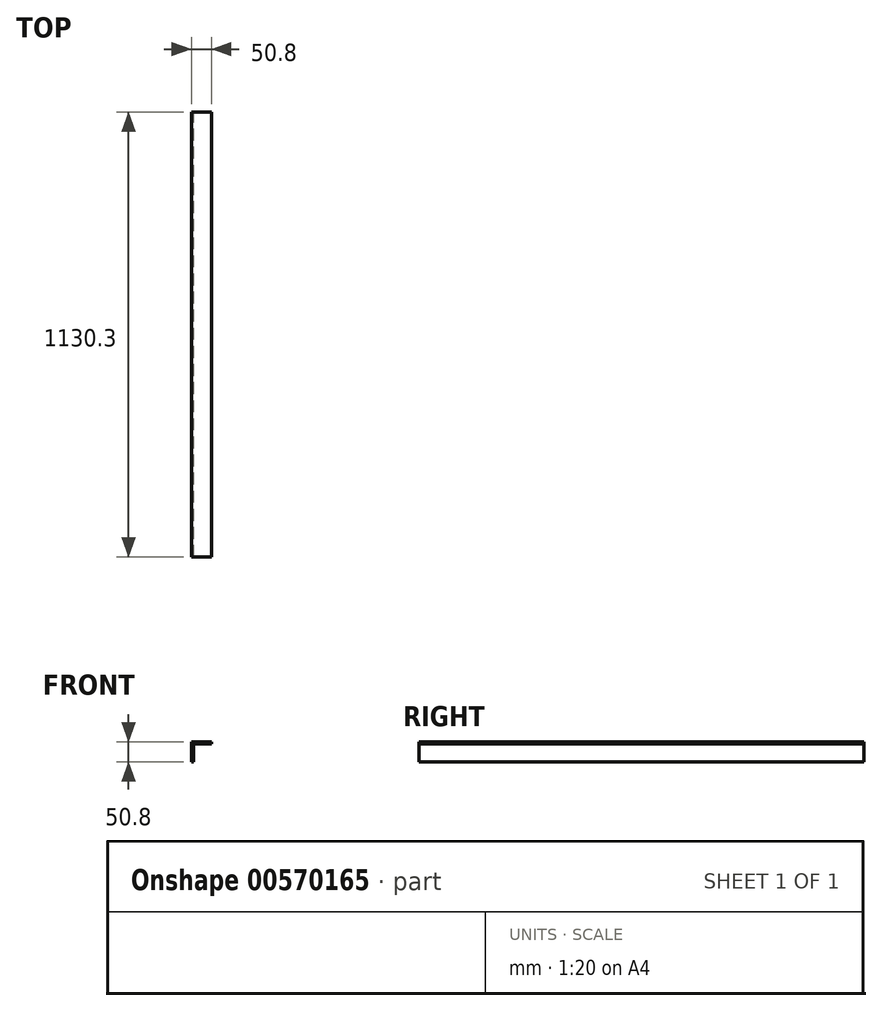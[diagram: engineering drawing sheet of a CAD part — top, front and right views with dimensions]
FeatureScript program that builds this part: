
annotation { "Feature Type Name" : "Feature", "Feature Type Description" : "" }
export const myFeature = defineFeature(function(context is Context, id is Id, definition is map)
    precondition{}
    {
        {
            var Q0;
            Q0=qCreatedBy(makeId("Front.planeOp"),FACE);
            var sketch = newSketch(context, id + "F0", { "sketchPlane" : qUnion([Q0])});
            skLineSegment(sketch, "E0", {"start": v(0, 0) * mm, "end": v(0, 50.8) * mm});
            skLineSegment(sketch, "E1", {"start": v(0, 50.8) * mm, "end": v(50.8, 50.8) * mm});
            skLineSegment(sketch, "E2", {"start": v(50.8, 50.8) * mm, "end": v(50.8, 46.04) * mm});
            skLineSegment(sketch, "E3", {"start": v(50.8, 46.04) * mm, "end": v(4.76, 46.04) * mm});
            skLineSegment(sketch, "E4", {"start": v(4.76, 46.04) * mm, "end": v(4.76, 0) * mm});
            skLineSegment(sketch, "E5", {"start": v(4.76, 0) * mm, "end": v(0, 0) * mm});
            skSolve(sketch);
        }
        {
            var Q0;
            Q0=makeQuery(id+"F0.imprint","IMPRINT",FACE,{"disambiguationData":[TD([[makeQuery(id+"F0.imprint","IMPRINT",EDGE,{"derivedFrom":sQuery(id+"F0.wireOp",EDGE,"E0")}),-1.0]])]});
            extrude(context, id + "F1", {"entities" : qUnion([Q0]), "depth" : 1130.3 * mm, "offsetDistance" : 25.4 * mm});
        }
    });
